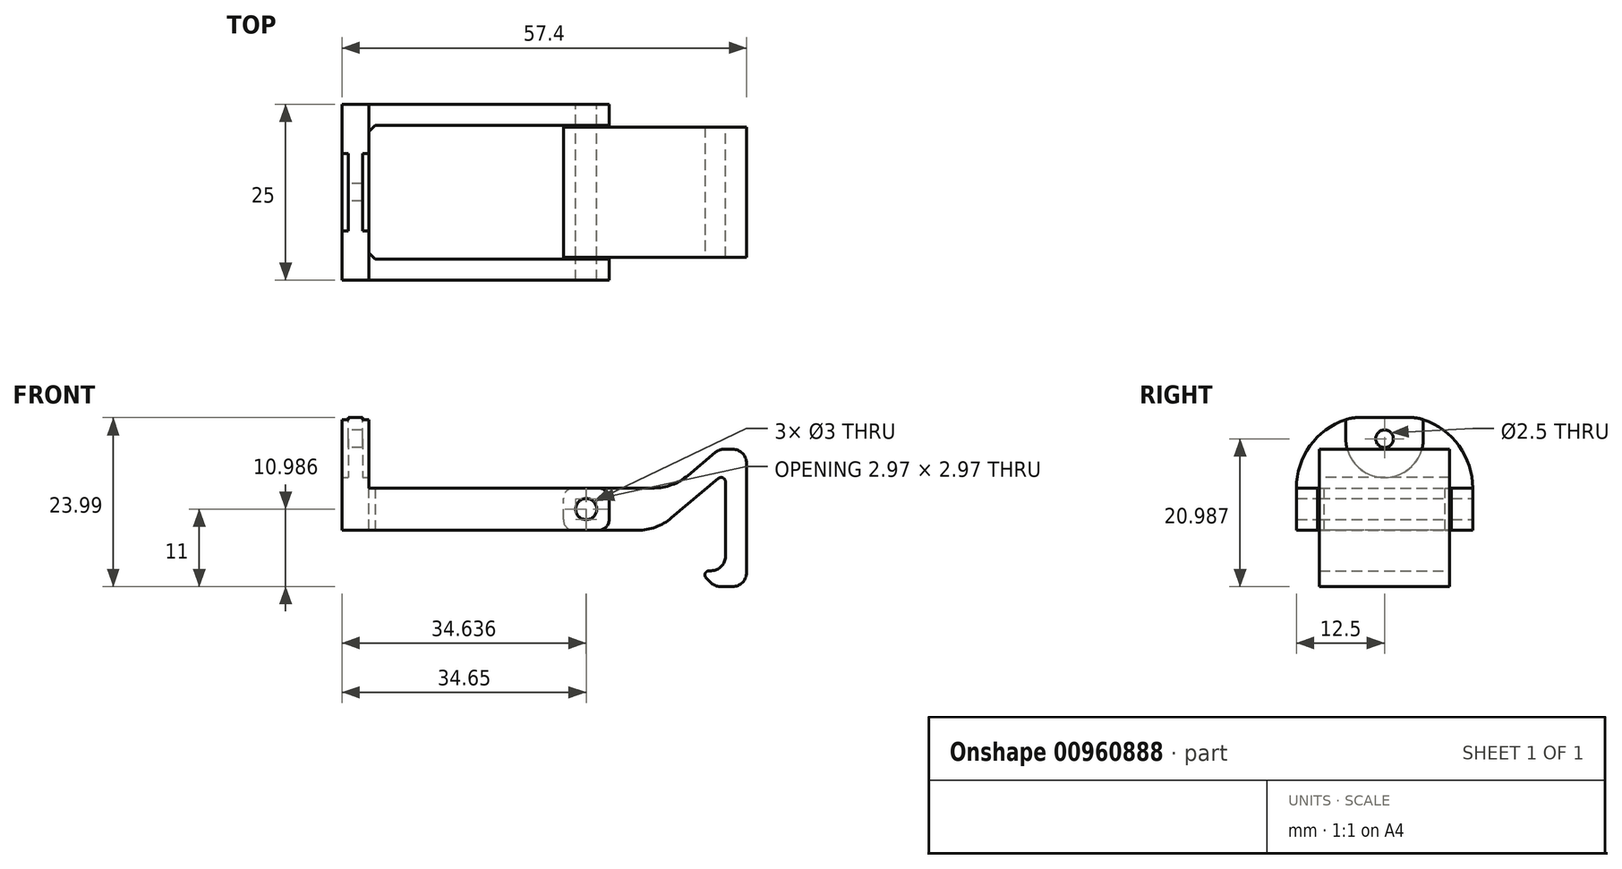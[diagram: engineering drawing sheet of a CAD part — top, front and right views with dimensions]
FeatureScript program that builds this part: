
annotation { "Feature Type Name" : "Feature", "Feature Type Description" : "" }
export const myFeature = defineFeature(function(context is Context, id is Id, definition is map)
    precondition{}
    {
        {
            var Q0;
            Q0=qCreatedBy(makeId("Right.planeOp"),FACE);
            var sketch = newSketch(context, id + "F0", { "sketchPlane" : qUnion([Q0])});
            skCircle(sketch, "E0", {"center": v(0, 12.99) * mm, "radius": 1.25 * mm});
            skLineSegment(sketch, "E1.bottom", {"start": v(-12.5, -0.01) * mm, "end": v(12.5, -0.01) * mm});
            skLineSegment(sketch, "E1.left", {"start": v(-12.5, -0.01) * mm, "end": v(-12.5, 7.99) * mm});
            skLineSegment(sketch, "E1.right", {"start": v(12.5, -0.01) * mm, "end": v(12.5, 7.99) * mm});
            skPoint(sketch, "E1.middle", {"position": v(0, 8) * mm});
            skLineSegment(sketch, "E2", {"start": v(12.5, 7.99) * mm, "end": v(-12.5, 7.99) * mm, "construction": true});
            skLineSegment(sketch, "E3", {"start": v(0, -0.01) * mm, "end": v(0, 15.99) * mm, "construction": true});
            skLineSegment(sketch, "E4.0", {"start": v(4.5, -0.01) * mm, "end": v(4.5, 15.99) * mm, "construction": true});
            skLineSegment(sketch, "E5.MirrorCS", {"start": v(-4.5, -0.01) * mm, "end": v(-4.5, 15.99) * mm, "construction": true});
            skArc(sketch, "E6", {"start": v(4.5, 15.99) * mm, "mid": v(10.16, 13.64) * mm, "end": v(12.5, 7.99) * mm});
            skArc(sketch, "E7", {"start": v(-12.5, 7.99) * mm, "mid": v(-10.16, 13.64) * mm, "end": v(-4.5, 15.99) * mm});
            skLineSegment(sketch, "E8", {"start": v(5.5, 12.99) * mm, "end": v(-5.5, 12.99) * mm, "construction": true});
            skLineSegment(sketch, "E9", {"start": v(-5.5, 12.99) * mm, "end": v(-5.5, 15.92) * mm});
            skLineSegment(sketch, "E10.MirrorCS", {"start": v(5.5, 12.99) * mm, "end": v(5.5, 15.92) * mm});
            skArc(sketch, "E11", {"start": v(5.5, 12.99) * mm, "mid": v(0, 7.49) * mm, "end": v(-5.5, 12.99) * mm});
            skLineSegment(sketch, "E12", {"start": v(4.5, 15.99) * mm, "end": v(-4.5, 15.99) * mm});
            skPoint(sketch, "E13.middle", {"position": v(0, -0.01) * mm});
            skLineSegment(sketch, "E14.bottom", {"start": v(-20, 22.99) * mm, "end": v(20, 22.99) * mm});
            skLineSegment(sketch, "E14.top", {"start": v(-20, -7.01) * mm, "end": v(20, -7.01) * mm});
            skLineSegment(sketch, "E14.left", {"start": v(-20, 22.99) * mm, "end": v(-20, -7.01) * mm});
            skLineSegment(sketch, "E14.right", {"start": v(20, 22.99) * mm, "end": v(20, -7.01) * mm});
            skCircle(sketch, "E15", {"center": v(0, 0) * mm, "radius": 2.5 * mm, "construction": true});
            skSolve(sketch);
        }
        {
            var Q0;
            Q0=qCreatedBy(makeId("Right.planeOp"),FACE);
            var sketch = newSketch(context, id + "F1", { "sketchPlane" : qUnion([Q0])});
            skLineSegment(sketch, "E16.0", {"start": v(9.5, -9.21) * mm, "end": v(12.5, -9.21) * mm});
            skLineSegment(sketch, "E16.1", {"start": v(-12.5, -9.21) * mm, "end": v(-9.5, -9.21) * mm});
            skCircle(sketch, "E17", {"center": v(0, 0) * mm, "radius": 2.5 * mm, "construction": true});
            skCircle(sketch, "E18.0", {"center": v(0, 12.99) * mm, "radius": 1.25 * mm});
            skLineSegment(sketch, "E19.0", {"start": v(4.5, 15.99) * mm, "end": v(-4.5, 15.99) * mm});
            skLineSegment(sketch, "E20.0", {"start": v(-20, 22.99) * mm, "end": v(20, 22.99) * mm});
            skLineSegment(sketch, "E20.1", {"start": v(-20, 22.99) * mm, "end": v(-20, -7.01) * mm});
            skLineSegment(sketch, "E20.2", {"start": v(20, 22.99) * mm, "end": v(20, -7.01) * mm});
            skLineSegment(sketch, "E20.3", {"start": v(-20, -7.01) * mm, "end": v(20, -7.01) * mm});
            skLineSegment(sketch, "E21.0", {"start": v(-12.5, -0.01) * mm, "end": v(12.5, -0.01) * mm});
            skLineSegment(sketch, "E22", {"start": v(-12.5, -0.01) * mm, "end": v(-12.5, 6) * mm});
            skLineSegment(sketch, "E23", {"start": v(12.5, -0.01) * mm, "end": v(12.5, 6) * mm});
            skArc(sketch, "E24", {"start": v(12.5, 6) * mm, "mid": v(10.25, 12.4) * mm, "end": v(4.5, 15.99) * mm});
            skArc(sketch, "E25", {"start": v(-12.5, 6) * mm, "mid": v(-10.25, 12.4) * mm, "end": v(-4.5, 15.99) * mm});
            skSolve(sketch);
        }
        {
            var Q0;
            Q0=qCreatedBy(makeId("Front.planeOp"),FACE);
            var sketch = newSketch(context, id + "F2", { "sketchPlane" : qUnion([Q0])});
            skPoint(sketch, "E26.middle", {"position": v(0, 8) * mm});
            skCircle(sketch, "E27", {"center": v(32.75, 3) * mm, "radius": 1.5 * mm});
            skArc(sketch, "E28", {"start": v(34.5, 0) * mm, "mid": v(35.56, 0.44) * mm, "end": v(36, 1.5) * mm});
            skArc(sketch, "E29.MirrorCS", {"start": v(34.5, 6) * mm, "mid": v(35.56, 5.56) * mm, "end": v(36, 4.5) * mm});
            skLineSegment(sketch, "E30", {"start": v(2, 6) * mm, "end": v(2, 16) * mm});
            skLineSegment(sketch, "E31", {"start": v(2, 16) * mm, "end": v(-2, 16) * mm});
            skLineSegment(sketch, "E32", {"start": v(-2, 16) * mm, "end": v(-2, 6) * mm});
            skLineSegment(sketch, "E33", {"start": v(-6.5, 0) * mm, "end": v(34.5, 0) * mm});
            skLineSegment(sketch, "E34", {"start": v(36, 4.5) * mm, "end": v(36, 1.5) * mm});
            skCircle(sketch, "E35", {"center": v(-4.75, 3) * mm, "radius": 1.5 * mm});
            skArc(sketch, "E36", {"start": v(-6.5, 6) * mm, "mid": v(-7.56, 5.56) * mm, "end": v(-8, 4.5) * mm});
            skArc(sketch, "E37.MirrorCS", {"start": v(-6.5, 0) * mm, "mid": v(-7.56, 0.44) * mm, "end": v(-8, 1.5) * mm});
            skLineSegment(sketch, "E38", {"start": v(-8, 1.5) * mm, "end": v(-8, 4.5) * mm});
            skLineSegment(sketch, "E39", {"start": v(34.5, 6) * mm, "end": v(2, 6) * mm});
            skLineSegment(sketch, "E40", {"start": v(-2, 6) * mm, "end": v(-6.5, 6) * mm});
            skSolve(sketch);
        }
        {
            var Q0;
            Q0=qCreatedBy(makeId("Top.planeOp"),FACE);
            var sketch = newSketch(context, id + "F3", { "sketchPlane" : qUnion([Q0])});
            skLineSegment(sketch, "E41.left", {"start": v(-2, 12.5) * mm, "end": v(-2, -12.5) * mm});
            skPoint(sketch, "E41.middle", {"position": v(31.25, 0) * mm});
            skLineSegment(sketch, "E42.0", {"start": v(2, 12.5) * mm, "end": v(2, -12.5) * mm});
            skLineSegment(sketch, "E43", {"start": v(-2, 0) * mm, "end": v(18.5, 0) * mm, "construction": true});
            skLineSegment(sketch, "E44.0", {"start": v(36, 12.5) * mm, "end": v(36, 9.5) * mm});
            skLineSegment(sketch, "E45.trimOffspring", {"start": v(36, -9.5) * mm, "end": v(36, -12.5) * mm});
            skLineSegment(sketch, "E46.bottom", {"start": v(44, 17.5) * mm, "end": v(-13, 17.5) * mm});
            skLineSegment(sketch, "E46.top", {"start": v(44, -17.5) * mm, "end": v(-13, -17.5) * mm});
            skLineSegment(sketch, "E46.left", {"start": v(44, 17.5) * mm, "end": v(44, -17.5) * mm});
            skLineSegment(sketch, "E46.right", {"start": v(-13, 17.5) * mm, "end": v(-13, -17.5) * mm});
            skPoint(sketch, "E46.middle", {"position": v(23, 0) * mm});
            skCircle(sketch, "E47", {"center": v(0, 0) * mm, "radius": 2.5 * mm, "construction": true});
            skLineSegment(sketch, "E48.0", {"start": v(36, -12.5) * mm, "end": v(-7.9, -12.5) * mm});
            skLineSegment(sketch, "E48.1", {"start": v(36, 12.5) * mm, "end": v(-7.9, 12.5) * mm});
            skLineSegment(sketch, "E48.2", {"start": v(-7.9, 9.5) * mm, "end": v(-2, 9.5) * mm});
            skLineSegment(sketch, "E48.3", {"start": v(-7.9, -9.5) * mm, "end": v(-2, -9.5) * mm});
            skCircle(sketch, "E48.4", {"center": v(23, 0) * mm, "radius": 2.5 * mm, "construction": true});
            skLineSegment(sketch, "E49", {"start": v(-7.9, 12.5) * mm, "end": v(-7.9, 9.5) * mm});
            skLineSegment(sketch, "E50", {"start": v(-7.9, -9.5) * mm, "end": v(-7.9, -12.5) * mm});
            skLineSegment(sketch, "E51", {"start": v(2, 9.5) * mm, "end": v(36, 9.5) * mm});
            skLineSegment(sketch, "E52", {"start": v(2, -9.5) * mm, "end": v(36, -9.5) * mm});
            skSolve(sketch);
        }
        {
            var Q0;
            Q0=qCreatedBy(makeId("Front.planeOp"),FACE);
            var sketch = newSketch(context, id + "F4", { "sketchPlane" : qUnion([Q0])});
            skCircle(sketch, "E53.0", {"center": v(32.75, 3) * mm, "radius": 1.5 * mm});
            skLineSegment(sketch, "E54.0", {"start": v(31, 0) * mm, "end": v(42.75, 0) * mm});
            skArc(sketch, "E54.1", {"start": v(31, 0) * mm, "mid": v(29.94, 0.44) * mm, "end": v(29.5, 1.5) * mm});
            skLineSegment(sketch, "E54.2", {"start": v(29.5, 1.5) * mm, "end": v(29.5, 4.5) * mm});
            skArc(sketch, "E54.3", {"start": v(31, 6) * mm, "mid": v(29.94, 5.56) * mm, "end": v(29.5, 4.5) * mm});
            skLineSegment(sketch, "E54.4", {"start": v(55.5, -8) * mm, "end": v(55.5, 11.5) * mm});
            skLineSegment(sketch, "E55", {"start": v(52.5, 8.18) * mm, "end": v(52.5, -5.75) * mm});
            skLineSegment(sketch, "E56", {"start": v(51.62, 11.5) * mm, "end": v(55.5, 11.5) * mm});
            skLineSegment(sketch, "E57", {"start": v(42.75, 0) * mm, "end": v(52.5, 8.18) * mm});
            skLineSegment(sketch, "E58", {"start": v(45.07, 6) * mm, "end": v(31, 6) * mm});
            skLineSegment(sketch, "E59", {"start": v(51.62, 11.5) * mm, "end": v(45.07, 6) * mm});
            skLineSegment(sketch, "E60", {"start": v(48.75, -5.75) * mm, "end": v(52.5, -5.75) * mm});
            skLineSegment(sketch, "E61", {"start": v(51, -8) * mm, "end": v(55.5, -8) * mm});
            skLineSegment(sketch, "E62.MirrorCS", {"start": v(48.75, -5.75) * mm, "end": v(51, -8) * mm});
            skSolve(sketch);
        }
        {
            var Q0;
            Q0=makeQuery(id+"F2.imprint","IMPRINT",FACE,{"disambiguationData":[TD([[makeQuery(id+"F2.imprint","IMPRINT",EDGE,{"derivedFrom":sQuery(id+"F2.wireOp",EDGE,"E27")}),-1.0]])]});
            extrude(context, id + "F5", {"entities" : qUnion([Q0]), "endBound" : BoundingType.SYMMETRIC, "depth" : 25 * mm, "offsetDistance" : 25 * mm});
        }
        {
            var Q0;
            {var subQ16=sQuery(id+"F3.wireOp",EDGE,"E44.0");Q0=makeQuery(id+"F3.imprint","IMPRINT",FACE,{"disambiguationData":[TD([[makeQuery(id+"F3.imprint","IMPRINT",EDGE,{"derivedFrom":subQ16}),1.0]])]});}
            var Q1;
            {var subQ0=sQuery(id+"F3.wireOp",EDGE,"E48.2");Q1=makeQuery(id+"F3.imprint","IMPRINT",FACE,{"disambiguationData":[TD([[makeQuery(id+"F3.imprint","IMPRINT",EDGE,{"derivedFrom":subQ0}),1.0]])]});}
            var Q2;
            {var subQ3=sQuery(id+"F3.wireOp",EDGE,"E48.3");Q2=makeQuery(id+"F3.imprint","IMPRINT",FACE,{"disambiguationData":[TD([[makeQuery(id+"F3.imprint","IMPRINT",EDGE,{"derivedFrom":subQ3}),-1.0]])]});}
            extrude(context, id + "F6", {"entities" : qUnion([Q0, Q1, Q2]), "operationType" : NewBodyOperationType.REMOVE, "depth" : 25 * mm, "offsetDistance" : 25 * mm});
        }
        {
            var Q0;
            Q0=makeQuery(id+"F0.imprint","IMPRINT",FACE,{"disambiguationData":[TD([[makeQuery(id+"F0.imprint","IMPRINT",EDGE,{"derivedFrom":sQuery(id+"F0.wireOp",EDGE,"E1.bottom")}),-1.0]])]});
            var Q1;
            Q1=makeQuery(id+"F0.imprint","IMPRINT",FACE,{"disambiguationData":[TD([[makeQuery(id+"F0.imprint","IMPRINT",EDGE,{"derivedFrom":sQuery(id+"F0.wireOp",EDGE,"E0")}),-1.0]])]});
            var Q2;
            Q2=makeQuery(id+"F0.imprint","IMPRINT",FACE,{"disambiguationData":[TD([[makeQuery(id+"F0.imprint","IMPRINT",EDGE,{"derivedFrom":sQuery(id+"F0.wireOp",EDGE,"E0")}),1.0]])]});
            extrude(context, id + "F7", {"entities" : qUnion([Q0, Q1, Q2]), "operationType" : NewBodyOperationType.REMOVE, "endBound" : BoundingType.SYMMETRIC, "oppositeDirection" : true, "depth" : 4 * mm, "offsetDistance" : 25 * mm});
        }
        {
            var Q0;
            Q0=makeQuery(id+"F0.imprint","IMPRINT",FACE,{"disambiguationData":[TD([[makeQuery(id+"F0.imprint","IMPRINT",EDGE,{"derivedFrom":sQuery(id+"F0.wireOp",EDGE,"E0")}),-1.0]])]});
            extrude(context, id + "F8", {"entities" : qUnion([Q0]), "operationType" : NewBodyOperationType.ADD, "endBound" : BoundingType.SYMMETRIC, "depth" : 2 * mm, "offsetDistance" : 25 * mm});
        }
        {
            var Q0;
            Q0=makeQuery(id+"F6.boolean.opBoolean","MERGE",FACE,{"derivedFrom":[makeQuery(id+"F5.opExtrude","SWEPT_FACE",FACE,{"disambiguationData":[OSD([sQuery(id+"F2.wireOp",EDGE,"E30")])]})],"fromTools":[makeQuery(id+"F6.opExtrude","SWEPT_FACE",FACE,{"disambiguationData":[OSD([sQuery(id+"F3.wireOp",EDGE,"E42.0")])]})]});
            extrude(context, id + "F9", {"entities" : qUnion([Q0]), "operationType" : NewBodyOperationType.REMOVE, "oppositeDirection" : true, "depth" : 0.1 * mm, "offsetDistance" : 25 * mm});
        }
        {
            var Q0;
            Q0=makeQuery(id+"F5.opExtrude","SWEPT_FACE",FACE,{"disambiguationData":[OSD([sQuery(id+"F2.wireOp",EDGE,"E32")])]});
            extrude(context, id + "F10", {"entities" : qUnion([Q0]), "operationType" : NewBodyOperationType.REMOVE, "oppositeDirection" : true, "depth" : 0.1 * mm, "offsetDistance" : 25 * mm});
        }
        {
            var Q0;
            Q0=makeQuery(id+"F9.boolean.opBoolean","COPY",EDGE,{"derivedFrom":makeQuery(id+"F9.opExtrude","CAP_EDGE",EDGE,{"disambiguationData":[OSD([sQuery(id+"F0.wireOp",EDGE,"E11")])],"isStart":false})});
            var Q1;
            Q1=makeQuery(id+"F10.boolean.opBoolean","COPY",EDGE,{"derivedFrom":makeQuery(id+"F10.opExtrude","CAP_EDGE",EDGE,{"disambiguationData":[OSD([sQuery(id+"F0.wireOp",EDGE,"E11")])],"isStart":false})});
            var Q2;
            Q2=makeQuery(id+"F10.boolean.opBoolean","COPY",EDGE,{"derivedFrom":makeQuery(id+"F10.opExtrude","CAP_EDGE",EDGE,{"disambiguationData":[OSD([sQuery(id+"F3.wireOp",EDGE,"E41.left"),sQuery(id+"F3.wireOp",EDGE,"E48.2")])],"isStart":false})});
            var Q3;
            Q3=makeQuery(id+"F10.boolean.opBoolean","COPY",EDGE,{"derivedFrom":makeQuery(id+"F10.opExtrude","CAP_EDGE",EDGE,{"disambiguationData":[OSD([sQuery(id+"F3.wireOp",EDGE,"E41.left"),sQuery(id+"F3.wireOp",EDGE,"E48.3")])],"isStart":false})});
            var Q4;
            Q4=makeQuery(id+"F9.boolean.opBoolean","COPY",EDGE,{"derivedFrom":makeQuery(id+"F9.opExtrude","CAP_EDGE",EDGE,{"disambiguationData":[OSD([sQuery(id+"F3.wireOp",EDGE,"E42.0"),sQuery(id+"F3.wireOp",EDGE,"E51")])],"isStart":false})});
            var Q5;
            Q5=makeQuery(id+"F9.boolean.opBoolean","COPY",EDGE,{"derivedFrom":makeQuery(id+"F9.opExtrude","CAP_EDGE",EDGE,{"disambiguationData":[OSD([sQuery(id+"F3.wireOp",EDGE,"E42.0"),sQuery(id+"F3.wireOp",EDGE,"E52")])],"isStart":false})});
            chamfer(context, id + "F11", {"entities" : qUnion([Q0, Q1, Q2, Q3, Q4, Q5]), "width" : 0.9 * mm, "tangentPropagation" : true});
        }
        {
            var Q0;
            Q0=makeQuery(id+"F4.imprint","IMPRINT",FACE,{"disambiguationData":[TD([[makeQuery(id+"F4.imprint","IMPRINT",EDGE,{"derivedFrom":sQuery(id+"F4.wireOp",EDGE,"E53.0")}),-1.0]])]});
            extrude(context, id + "F12", {"entities" : qUnion([Q0]), "endBound" : BoundingType.SYMMETRIC, "depth" : 18.5 * mm, "offsetDistance" : 25 * mm});
        }
        {
            var Q0;
            Q0=makeQuery(id+"F12.opExtrude","SWEPT_EDGE",EDGE,{"disambiguationData":[OSD([sQuery(id+"F4.wireOp",EDGE,"E56"),sQuery(id+"F4.wireOp",EDGE,"E59")])]});
            var Q1;
            Q1=makeQuery(id+"F12.opExtrude","SWEPT_EDGE",EDGE,{"disambiguationData":[OSD([sQuery(id+"F4.wireOp",EDGE,"E54.4"),sQuery(id+"F4.wireOp",EDGE,"E56")])]});
            var Q2;
            Q2=makeQuery(id+"F12.opExtrude","SWEPT_EDGE",EDGE,{"disambiguationData":[OSD([sQuery(id+"F4.wireOp",EDGE,"E54.4"),sQuery(id+"F4.wireOp",EDGE,"E61")])]});
            var Q3;
            Q3=makeQuery(id+"F12.opExtrude","SWEPT_EDGE",EDGE,{"disambiguationData":[OSD([sQuery(id+"F4.wireOp",EDGE,"E61"),sQuery(id+"F4.wireOp",EDGE,"E62.MirrorCS")])]});
            var Q4;
            Q4=makeQuery(id+"F12.opExtrude","SWEPT_EDGE",EDGE,{"disambiguationData":[OSD([sQuery(id+"F4.wireOp",EDGE,"E55"),sQuery(id+"F4.wireOp",EDGE,"E60")])]});
            fillet(context, id + "F13", {"entities" : qUnion([Q0, Q1, Q2, Q3, Q4]), "tangentPropagation" : true, "radius" : 2 * mm, "defaultsChanged" : false, "vertexSettings" : [], "allowEdgeOverflow" : false});
        }
        {
            var Q0;
            Q0=makeQuery(id+"F12.opExtrude","SWEPT_EDGE",EDGE,{"disambiguationData":[OSD([sQuery(id+"F4.wireOp",EDGE,"E58"),sQuery(id+"F4.wireOp",EDGE,"E59")])]});
            var Q1;
            Q1=makeQuery(id+"F12.opExtrude","SWEPT_EDGE",EDGE,{"disambiguationData":[OSD([sQuery(id+"F4.wireOp",EDGE,"E54.0"),sQuery(id+"F4.wireOp",EDGE,"E57")])]});
            fillet(context, id + "F14", {"entities" : qUnion([Q0, Q1]), "tangentPropagation" : true, "radius" : 7.5 * mm, "defaultsChanged" : true, "vertexSettings" : [], "allowEdgeOverflow" : false});
        }
        {
            var Q0;
            Q0=makeQuery(id+"F12.opExtrude","SWEPT_EDGE",EDGE,{"disambiguationData":[OSD([sQuery(id+"F4.wireOp",EDGE,"E55"),sQuery(id+"F4.wireOp",EDGE,"E57")])]});
            var Q1;
            Q1=makeQuery(id+"F12.opExtrude","SWEPT_EDGE",EDGE,{"disambiguationData":[OSD([sQuery(id+"F4.wireOp",EDGE,"E60"),sQuery(id+"F4.wireOp",EDGE,"E62.MirrorCS")])]});
            fillet(context, id + "F15", {"entities" : qUnion([Q0, Q1]), "tangentPropagation" : true, "radius" : 0.6 * mm, "defaultsChanged" : true, "vertexSettings" : [], "allowEdgeOverflow" : false});
        }
        {
            var Q0;
            Q0=makeQuery(id+"F1.imprint","IMPRINT",FACE,{"disambiguationData":[TD([[makeQuery(id+"F1.imprint","IMPRINT",EDGE,{"derivedFrom":sQuery(id+"F1.wireOp",EDGE,"E19.0")}),-1.0]])]});
            extrude(context, id + "F16", {"entities" : qUnion([Q0]), "operationType" : NewBodyOperationType.REMOVE, "endBound" : BoundingType.SYMMETRIC, "oppositeDirection" : true, "depth" : 25 * mm, "offsetDistance" : 25 * mm});
        }
        {
            var Q0;
            Q0=makeQuery(id+"F16.boolean.opBoolean","MERGE",EDGE,{"derivedFrom":[makeQuery(id+"F8.opExtrude","SWEPT_EDGE",EDGE,{"disambiguationData":[OSD([sQuery(id+"F0.wireOp",EDGE,"E7"),sQuery(id+"F0.wireOp",EDGE,"E12")])]})],"fromTools":[makeQuery(id+"F16.opExtrude","SWEPT_EDGE",EDGE,{"disambiguationData":[OSD([sQuery(id+"F1.wireOp",EDGE,"E19.0"),sQuery(id+"F1.wireOp",EDGE,"E25")])]})]});
            var Q1;
            Q1=makeQuery(id+"F16.boolean.opBoolean","MERGE",EDGE,{"derivedFrom":[makeQuery(id+"F8.opExtrude","SWEPT_EDGE",EDGE,{"disambiguationData":[OSD([sQuery(id+"F0.wireOp",EDGE,"E6"),sQuery(id+"F0.wireOp",EDGE,"E12")])]})],"fromTools":[makeQuery(id+"F16.opExtrude","SWEPT_EDGE",EDGE,{"disambiguationData":[OSD([sQuery(id+"F1.wireOp",EDGE,"E19.0"),sQuery(id+"F1.wireOp",EDGE,"E24")])]})]});
            fillet(context, id + "F17", {"entities" : qUnion([Q0, Q1]), "tangentPropagation" : true, "radius" : 5 * mm, "defaultsChanged" : false, "vertexSettings" : [], "allowEdgeOverflow" : false});
        }
    });
